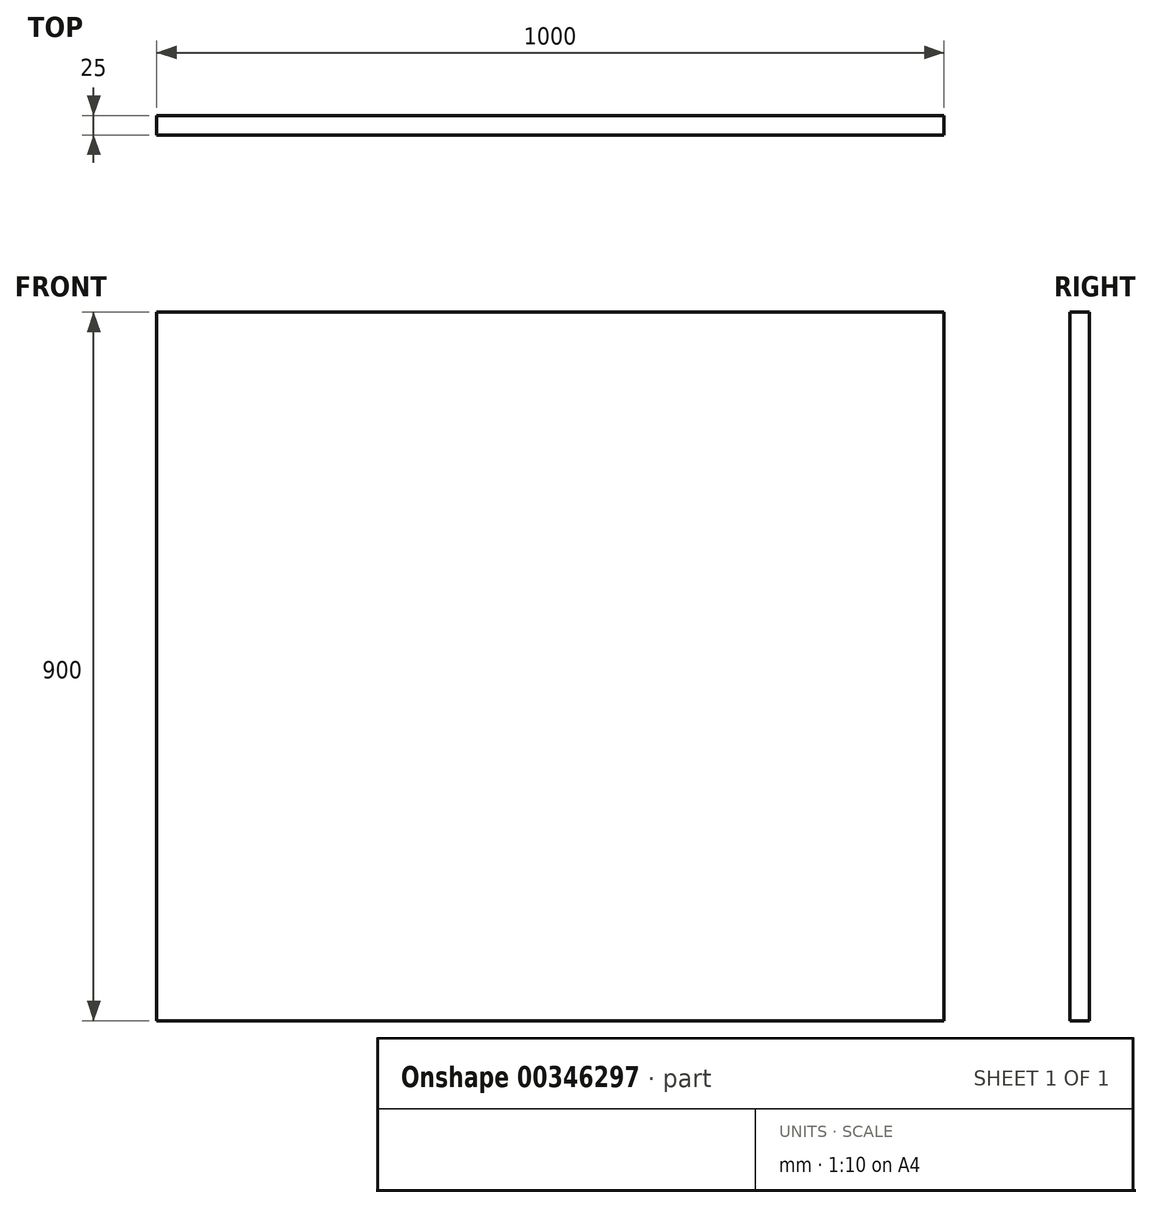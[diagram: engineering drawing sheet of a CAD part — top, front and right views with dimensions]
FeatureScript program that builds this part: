
annotation { "Feature Type Name" : "Feature", "Feature Type Description" : "" }
export const myFeature = defineFeature(function(context is Context, id is Id, definition is map)
    precondition{}
    {
        {
            var Q0;
            Q0=qCreatedBy(makeId("Front.planeOp"),FACE);
            var sketch = newSketch(context, id + "F0", { "sketchPlane" : qUnion([Q0])});
            skLineSegment(sketch, "E0.bottom", {"start": v(-500, 450) * mm, "end": v(500, 450) * mm});
            skLineSegment(sketch, "E0.top", {"start": v(-500, -450) * mm, "end": v(500, -450) * mm});
            skLineSegment(sketch, "E0.left", {"start": v(-500, 450) * mm, "end": v(-500, -450) * mm});
            skLineSegment(sketch, "E0.right", {"start": v(500, 450) * mm, "end": v(500, -450) * mm});
            skPoint(sketch, "E0.middle", {"position": v(0, 0) * mm});
            skSolve(sketch);
        }
        {
            var Q0;
            Q0 = qSketchRegion(id + "F0", true);
            extrude(context, id + "F1", {"entities" : qUnion([Q0]), "depth" : 25 * mm});
        }
    });
